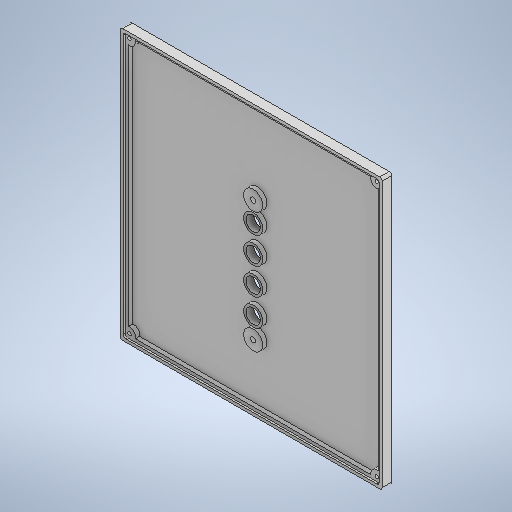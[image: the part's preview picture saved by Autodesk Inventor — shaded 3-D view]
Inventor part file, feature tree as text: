
AUTODESK INVENTOR PART (.ipt)
format: ipt  version: 2025 (Build 290162000, 162)  size: 349,696 bytes
history: native  units: in
note: dims shown in document units (in); Inventor stores cm internally (conversion verified against a paired STEP export)
features: extrude x7, sketch x7, fillet x1
ambient origin geometry x8: Origin, YZ Plane, XZ Plane, XY Plane, X Axis, Y Axis, Z Axis, Center Point
bodies: Solid1 (feature_tree)
feature tree (15):
  extrude  "Extrusion1"  Depth=8.937in
  extrude  "Extrusion2"  Depth=8.4685in
  extrude  "Extrusion3"  Depth=0.063in TaperAngle=0.0deg
  fillet  "Fillet1"  Radius=8.2677in
  extrude  "Extrusion4"  Depth=0.1378in TaperAngle=0.0deg
  extrude  "Extrusion5"  Depth=0.3937in
  extrude  "Extrusion6"  Depth=0.3937in
  extrude  "Extrusion7"  Depth=0.3937in
  sketch  "Sketch1"  dims[d0=8.6614in d1=8.937in]
  sketch  "Sketch2"  dims[d2=0.315in d3=0.0in d4=8.4685in]
  sketch  "Sketch3"  dims[d5=8.7441in d6=0.063in d7=0.0in d8=8.2677in]
  sketch  "Sketch4"  dims[d9=8.5433in d10=0.1378in d11=0.0in]
  sketch  "Sketch5"  dims[d12=0.0787in d13=0.3937in]
  sketch  "Sketch6"  dims[d14=0.3937in d15=8.4567in]
  sketch  "Sketch7"  dims[d16=0.1437in d17=0.3937in d18=8.1811in d19=0.1437in d20=0.3937in d21=0.1437in d22=8.4567in d23=8.1811in d24=0.1437in d25=0.1378in d26=0.0in d27=0.1102in d28=0.1102in d29=0.1102in d30=0.1102in d31=0.1378in d32=0.0in d33=0.6299in d34=2.0179in d35=0.6299in d36=2.7244in d37=0.6299in d38=2.6988in d39=0.6299in d40=0.6299in d41=0.6299in d42=0.8858in d43=0.8858in d44=0.8858in d45=0.1378in d46=0.0in d47=0.1654in d48=0.4724in d49=0.4724in d50=0.4724in d51=0.4724in d52=0.1654in d53=0.0in d54=0.0in]
